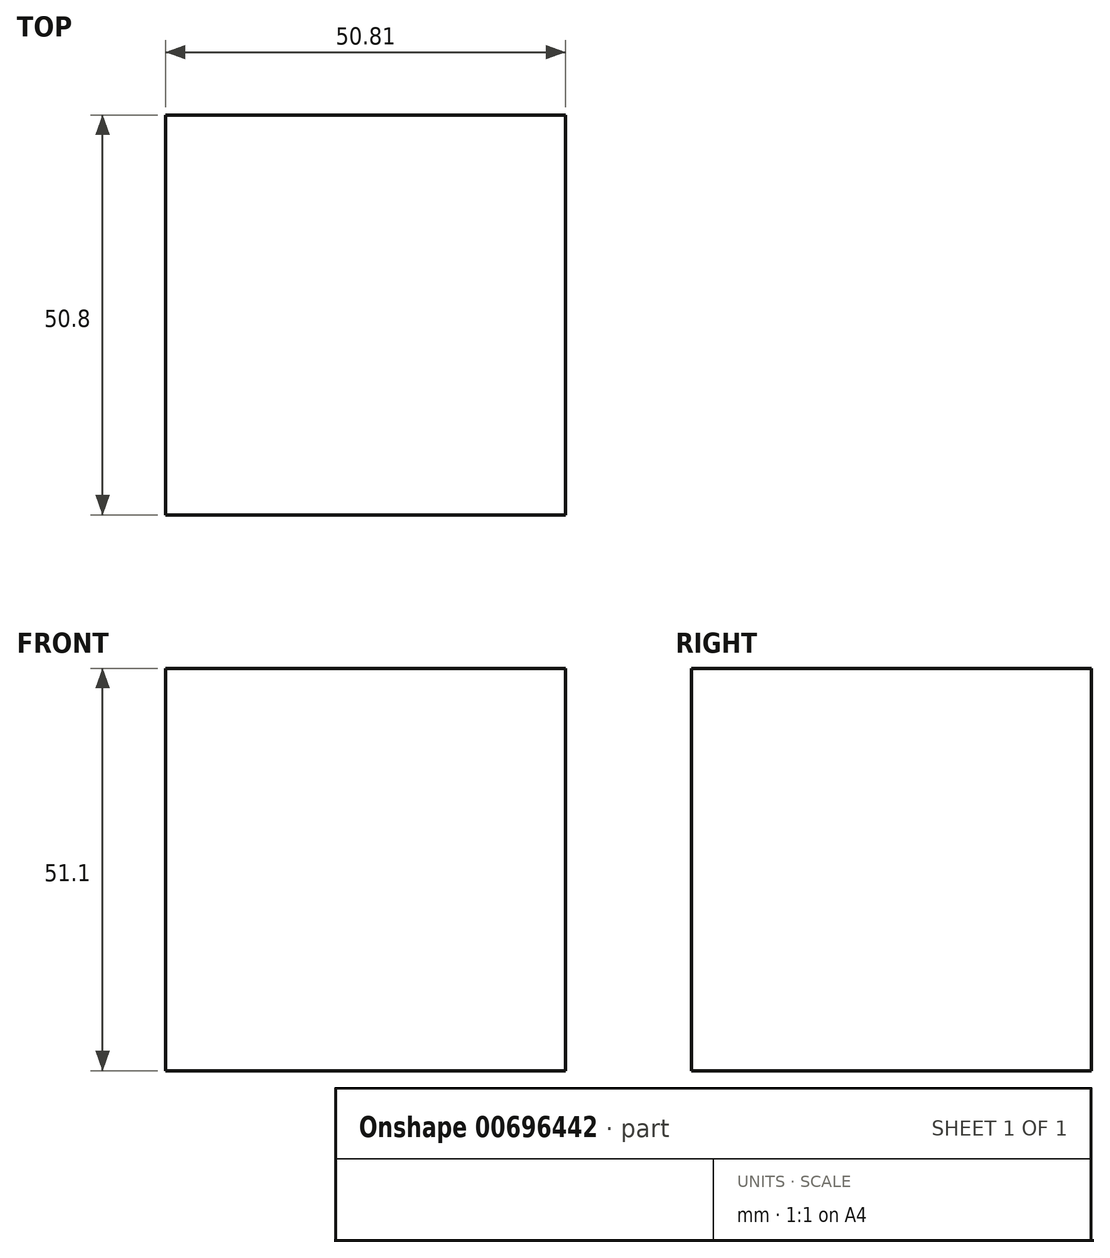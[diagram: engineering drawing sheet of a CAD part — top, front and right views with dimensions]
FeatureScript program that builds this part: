
annotation { "Feature Type Name" : "Feature", "Feature Type Description" : "" }
export const myFeature = defineFeature(function(context is Context, id is Id, definition is map)
    precondition{}
    {
        {
            var Q0;
            Q0=qCreatedBy(makeId("Front.planeOp"),FACE);
            var sketch = newSketch(context, id + "F0", { "sketchPlane" : qUnion([Q0])});
            skLineSegment(sketch, "E0.bottom", {"start": v(0, 0) * mm, "end": v(-50.8, 0) * mm});
            skLineSegment(sketch, "E0.top", {"start": v(0, 51.1) * mm, "end": v(-50.8, 51.1) * mm});
            skLineSegment(sketch, "E0.left", {"start": v(0, 0) * mm, "end": v(0, 51.1) * mm});
            skLineSegment(sketch, "E0.right", {"start": v(-50.8, 0) * mm, "end": v(-50.8, 51.1) * mm});
            skSolve(sketch);
        }
        {
            var Q0;
            Q0=makeQuery(id+"F0.imprint","IMPRINT",FACE,{"disambiguationData":[TD([[makeQuery(id+"F0.imprint","IMPRINT",EDGE,{"derivedFrom":sQuery(id+"F0.wireOp",EDGE,"E0.bottom")}),-1.0]])]});
            extrude(context, id + "F1", {"entities" : qUnion([Q0]), "depth" : 50.8 * mm, "offsetDistance" : 25.4 * mm});
        }
    });
